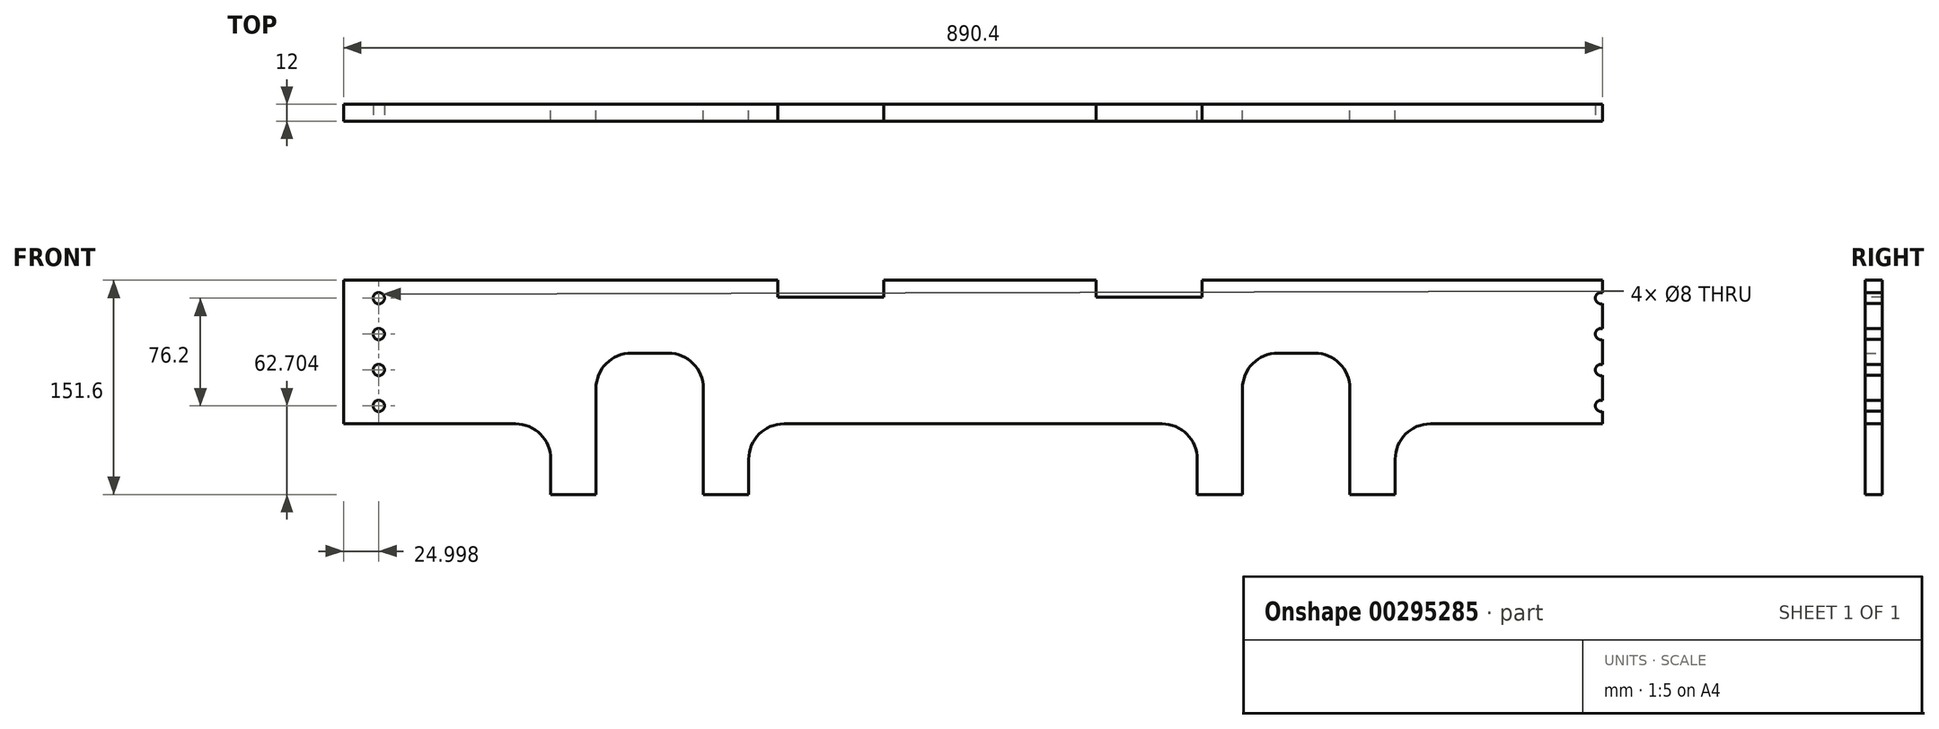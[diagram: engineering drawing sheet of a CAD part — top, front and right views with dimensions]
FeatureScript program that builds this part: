
annotation { "Feature Type Name" : "Feature", "Feature Type Description" : "" }
export const myFeature = defineFeature(function(context is Context, id is Id, definition is map)
    precondition{}
    {
        {
            var Q0;
            Q0=qCreatedBy(makeId("Front.planeOp"),FACE);
            var sketch = newSketch(context, id + "F0", { "sketchPlane" : qUnion([Q0])});
            skLineSegment(sketch, "E0", {"start": v(-558, 96.8) * mm, "end": v(332.4, 96.8) * mm});
            skLineSegment(sketch, "E1", {"start": v(332.4, 96.8) * mm, "end": v(332.4, -4.8) * mm});
            skLineSegment(sketch, "E2", {"start": v(332.4, -4.8) * mm, "end": v(210.8, -4.8) * mm});
            skLineSegment(sketch, "E3", {"start": v(185.8, -29.8) * mm, "end": v(185.8, -54.8) * mm});
            skLineSegment(sketch, "E4", {"start": v(185.8, -54.8) * mm, "end": v(153.8, -54.8) * mm});
            skLineSegment(sketch, "E5", {"start": v(153.8, -54.8) * mm, "end": v(153.8, 20.2) * mm});
            skLineSegment(sketch, "E6", {"start": v(128.8, 45.2) * mm, "end": v(102.8, 45.2) * mm});
            skLineSegment(sketch, "E7", {"start": v(77.8, 20.2) * mm, "end": v(77.8, -54.8) * mm});
            skLineSegment(sketch, "E8", {"start": v(77.8, -54.8) * mm, "end": v(45.8, -54.8) * mm});
            skLineSegment(sketch, "E9", {"start": v(-303.4, -54.8) * mm, "end": v(-303.4, 20.2) * mm});
            skLineSegment(sketch, "E10", {"start": v(-328.4, 45.2) * mm, "end": v(-354.4, 45.2) * mm});
            skLineSegment(sketch, "E11", {"start": v(-379.4, 20.2) * mm, "end": v(-379.4, -54.8) * mm});
            skLineSegment(sketch, "E12", {"start": v(-379.4, -54.8) * mm, "end": v(-411.4, -54.8) * mm});
            skLineSegment(sketch, "E13", {"start": v(-411.4, -54.8) * mm, "end": v(-411.4, -29.8) * mm});
            skLineSegment(sketch, "E14", {"start": v(-558, -4.8) * mm, "end": v(-558, 96.8) * mm});
            skPoint(sketch, "E15.visualSharp", {"position": v(-303.4, 45.2) * mm});
            skArc(sketch, "E15.filletArc", {"start": v(-303.4, 20.2) * mm, "mid": v(-310.72, 37.87) * mm, "end": v(-328.4, 45.2) * mm});
            skPoint(sketch, "E16.visualSharp", {"position": v(-379.4, 45.2) * mm});
            skArc(sketch, "E16.filletArc", {"start": v(-354.4, 45.2) * mm, "mid": v(-372.08, 37.87) * mm, "end": v(-379.4, 20.2) * mm});
            skPoint(sketch, "E17.visualSharp", {"position": v(185.8, -4.8) * mm});
            skArc(sketch, "E17.filletArc", {"start": v(210.8, -4.8) * mm, "mid": v(193.12, -12.13) * mm, "end": v(185.8, -29.8) * mm});
            skPoint(sketch, "E18.visualSharp", {"position": v(153.8, 45.2) * mm});
            skArc(sketch, "E18.filletArc", {"start": v(153.8, 20.2) * mm, "mid": v(146.48, 37.87) * mm, "end": v(128.8, 45.2) * mm});
            skPoint(sketch, "E19.visualSharp", {"position": v(77.8, 45.2) * mm});
            skArc(sketch, "E19.filletArc", {"start": v(102.8, 45.2) * mm, "mid": v(85.12, 37.87) * mm, "end": v(77.8, 20.2) * mm});
            skLineSegment(sketch, "E20", {"start": v(-558, -4.8) * mm, "end": v(-436.4, -4.8) * mm});
            skPoint(sketch, "E21.visualSharp", {"position": v(-411.4, -4.8) * mm});
            skArc(sketch, "E21.filletArc", {"start": v(-411.4, -29.8) * mm, "mid": v(-418.72, -12.13) * mm, "end": v(-436.4, -4.8) * mm});
            skLineSegment(sketch, "E22", {"start": v(-271.4, -54.8) * mm, "end": v(-271.4, -29.8) * mm});
            skLineSegment(sketch, "E23", {"start": v(-246.4, -4.8) * mm, "end": v(20.8, -4.8) * mm});
            skLineSegment(sketch, "E24", {"start": v(45.8, -29.8) * mm, "end": v(45.8, -54.8) * mm});
            skLineSegment(sketch, "E25.trimOffspring", {"start": v(-271.4, -54.8) * mm, "end": v(-303.4, -54.8) * mm});
            skPoint(sketch, "E26.visualSharp", {"position": v(-271.4, -4.8) * mm});
            skArc(sketch, "E26.filletArc", {"start": v(-246.4, -4.8) * mm, "mid": v(-264.08, -12.13) * mm, "end": v(-271.4, -29.8) * mm});
            skPoint(sketch, "E27.visualSharp", {"position": v(45.8, -4.8) * mm});
            skArc(sketch, "E27.filletArc", {"start": v(45.8, -29.8) * mm, "mid": v(38.48, -12.13) * mm, "end": v(20.8, -4.8) * mm});
            skSolve(sketch);
        }
        {
            var Q0;
            Q0=makeQuery(id+"F0.imprint","IMPRINT",FACE,{"disambiguationData":[TD([[makeQuery(id+"F0.imprint","IMPRINT",EDGE,{"derivedFrom":sQuery(id+"F0.wireOp",EDGE,"E0")}),-1.0]])]});
            extrude(context, id + "F1", {"entities" : qUnion([Q0]), "depth" : 12 * mm});
        }
        {
            var Q0;
            Q0=makeQuery(id+"F1.opExtrude","CAP_FACE",FACE,{"disambiguationData":[OSD([sQuery(id+"F0.wireOp",EDGE,"E0"),sQuery(id+"F0.wireOp",EDGE,"E1"),sQuery(id+"F0.wireOp",EDGE,"E2"),sQuery(id+"F0.wireOp",EDGE,"E3"),sQuery(id+"F0.wireOp",EDGE,"E4"),sQuery(id+"F0.wireOp",EDGE,"E5"),sQuery(id+"F0.wireOp",EDGE,"E6"),sQuery(id+"F0.wireOp",EDGE,"E7"),sQuery(id+"F0.wireOp",EDGE,"E8"),sQuery(id+"F0.wireOp",EDGE,"E9"),sQuery(id+"F0.wireOp",EDGE,"E10"),sQuery(id+"F0.wireOp",EDGE,"E11"),sQuery(id+"F0.wireOp",EDGE,"E12"),sQuery(id+"F0.wireOp",EDGE,"E13"),sQuery(id+"F0.wireOp",EDGE,"E14"),sQuery(id+"F0.wireOp",EDGE,"E15.filletArc"),sQuery(id+"F0.wireOp",EDGE,"E16.filletArc"),sQuery(id+"F0.wireOp",EDGE,"E17.filletArc"),sQuery(id+"F0.wireOp",EDGE,"E18.filletArc"),sQuery(id+"F0.wireOp",EDGE,"E19.filletArc"),sQuery(id+"F0.wireOp",EDGE,"E20"),sQuery(id+"F0.wireOp",EDGE,"E21.filletArc"),sQuery(id+"F0.wireOp",EDGE,"E22"),sQuery(id+"F0.wireOp",EDGE,"E23"),sQuery(id+"F0.wireOp",EDGE,"E24"),sQuery(id+"F0.wireOp",EDGE,"E25.trimOffspring"),sQuery(id+"F0.wireOp",EDGE,"E26.filletArc"),sQuery(id+"F0.wireOp",EDGE,"E27.filletArc")])],"isStart":false});
            var sketch = newSketch(context, id + "F2", { "sketchPlane" : qUnion([Q0])});
            skPoint(sketch, "E28", {"position": v(-533, 84.1) * mm});
            skPoint(sketch, "E29", {"position": v(-533, 58.7) * mm});
            skPoint(sketch, "E30", {"position": v(-533, 33.3) * mm});
            skPoint(sketch, "E31", {"position": v(-533, 7.9) * mm});
            skPoint(sketch, "E32", {"position": v(-395.4, -48.8) * mm});
            skPoint(sketch, "E33", {"position": v(-287.4, -48.8) * mm});
            skLineSegment(sketch, "E34", {"start": v(-100.8, -4.8) * mm, "end": v(-100.8, 96.8) * mm});
            skPoint(sketch, "E35.MirrorP", {"position": v(85.8, -48.8) * mm});
            skPoint(sketch, "E36.MirrorP", {"position": v(331.4, 58.7) * mm});
            skPoint(sketch, "E37.MirrorP", {"position": v(193.8, -48.8) * mm});
            skPoint(sketch, "E38.MirrorP", {"position": v(331.4, 84.1) * mm});
            skPoint(sketch, "E39.MirrorP", {"position": v(331.4, 7.9) * mm});
            skPoint(sketch, "E40.MirrorP", {"position": v(331.4, 33.3) * mm});
            skSolve(sketch);
        }
        {
            var Q0;
            Q0=sQuery(id+"F2.wireOp",VERTEX,"E28");
            var Q1;
            Q1=sQuery(id+"F2.wireOp",VERTEX,"E29");
            var Q2;
            Q2=sQuery(id+"F2.wireOp",VERTEX,"E30");
            var Q3;
            Q3=sQuery(id+"F2.wireOp",VERTEX,"E31");
            var Q4;
            Q4=sQuery(id+"F2.wireOp",VERTEX,"E38.MirrorP");
            var Q5;
            Q5=sQuery(id+"F2.wireOp",VERTEX,"E36.MirrorP");
            var Q6;
            Q6=sQuery(id+"F2.wireOp",VERTEX,"E40.MirrorP");
            var Q7;
            Q7=sQuery(id+"F2.wireOp",VERTEX,"E39.MirrorP");
            var Q8;
            Q8=makeQuery(id+"F1.opExtrude","SWEPT_BODY",BODY,{"disambiguationData":[OSD([sQuery(id+"F0.wireOp",EDGE,"E0"),sQuery(id+"F0.wireOp",EDGE,"E1"),sQuery(id+"F0.wireOp",EDGE,"E2"),sQuery(id+"F0.wireOp",EDGE,"E3"),sQuery(id+"F0.wireOp",EDGE,"E4"),sQuery(id+"F0.wireOp",EDGE,"E5"),sQuery(id+"F0.wireOp",EDGE,"E6"),sQuery(id+"F0.wireOp",EDGE,"E7"),sQuery(id+"F0.wireOp",EDGE,"E8"),sQuery(id+"F0.wireOp",EDGE,"E9"),sQuery(id+"F0.wireOp",EDGE,"E10"),sQuery(id+"F0.wireOp",EDGE,"E11"),sQuery(id+"F0.wireOp",EDGE,"E12"),sQuery(id+"F0.wireOp",EDGE,"E13"),sQuery(id+"F0.wireOp",EDGE,"E14"),sQuery(id+"F0.wireOp",EDGE,"E15.filletArc"),sQuery(id+"F0.wireOp",EDGE,"E16.filletArc"),sQuery(id+"F0.wireOp",EDGE,"E17.filletArc"),sQuery(id+"F0.wireOp",EDGE,"E18.filletArc"),sQuery(id+"F0.wireOp",EDGE,"E19.filletArc"),sQuery(id+"F0.wireOp",EDGE,"E20"),sQuery(id+"F0.wireOp",EDGE,"E21.filletArc"),sQuery(id+"F0.wireOp",EDGE,"E22"),sQuery(id+"F0.wireOp",EDGE,"E23"),sQuery(id+"F0.wireOp",EDGE,"E24"),sQuery(id+"F0.wireOp",EDGE,"E25.trimOffspring"),sQuery(id+"F0.wireOp",EDGE,"E26.filletArc"),sQuery(id+"F0.wireOp",EDGE,"E27.filletArc")])]});
            hole(context, id + "F3", {"style" : HoleStyle.SIMPLE, "endStyle" : HoleEndStyle.THROUGH, "standardTappedOrClearance" : lookupTablePath({ "standard" : "ISO", "size" : "8", "type" : "Drilled" }), "standardBlindInLast" : lookupTablePath({ "standard" : "ISO", "size" : "8", "type" : "Drilled" }), "holeDiameter" : 8 * mm, "tappedDepth" : 12 * mm, "tapClearance" : 3, "locations" : qUnion([Q0, Q1, Q2, Q3, Q4, Q5, Q6, Q7]), "scope" : qUnion([Q8])});
        }
        {
            var Q0;
            Q0=makeQuery(id+"F1.opExtrude","CAP_FACE",FACE,{"disambiguationData":[OSD([sQuery(id+"F0.wireOp",EDGE,"E0"),sQuery(id+"F0.wireOp",EDGE,"E1"),sQuery(id+"F0.wireOp",EDGE,"E2"),sQuery(id+"F0.wireOp",EDGE,"E3"),sQuery(id+"F0.wireOp",EDGE,"E4"),sQuery(id+"F0.wireOp",EDGE,"E5"),sQuery(id+"F0.wireOp",EDGE,"E6"),sQuery(id+"F0.wireOp",EDGE,"E7"),sQuery(id+"F0.wireOp",EDGE,"E8"),sQuery(id+"F0.wireOp",EDGE,"E9"),sQuery(id+"F0.wireOp",EDGE,"E10"),sQuery(id+"F0.wireOp",EDGE,"E11"),sQuery(id+"F0.wireOp",EDGE,"E12"),sQuery(id+"F0.wireOp",EDGE,"E13"),sQuery(id+"F0.wireOp",EDGE,"E14"),sQuery(id+"F0.wireOp",EDGE,"E15.filletArc"),sQuery(id+"F0.wireOp",EDGE,"E16.filletArc"),sQuery(id+"F0.wireOp",EDGE,"E17.filletArc"),sQuery(id+"F0.wireOp",EDGE,"E18.filletArc"),sQuery(id+"F0.wireOp",EDGE,"E19.filletArc"),sQuery(id+"F0.wireOp",EDGE,"E20"),sQuery(id+"F0.wireOp",EDGE,"E21.filletArc"),sQuery(id+"F0.wireOp",EDGE,"E22"),sQuery(id+"F0.wireOp",EDGE,"E23"),sQuery(id+"F0.wireOp",EDGE,"E24"),sQuery(id+"F0.wireOp",EDGE,"E25.trimOffspring"),sQuery(id+"F0.wireOp",EDGE,"E26.filletArc"),sQuery(id+"F0.wireOp",EDGE,"E27.filletArc")])],"isStart":false});
            var sketch = newSketch(context, id + "F4", { "sketchPlane" : qUnion([Q0])});
            skLineSegment(sketch, "E41.bottom", {"start": v(-250.8, 96.8) * mm, "end": v(-175.8, 96.8) * mm});
            skLineSegment(sketch, "E41.top", {"start": v(-250.8, 84.8) * mm, "end": v(-175.8, 84.8) * mm});
            skLineSegment(sketch, "E41.left", {"start": v(-250.8, 96.8) * mm, "end": v(-250.8, 84.8) * mm});
            skLineSegment(sketch, "E41.right", {"start": v(-175.8, 96.8) * mm, "end": v(-175.8, 84.8) * mm});
            skLineSegment(sketch, "E42.bottom", {"start": v(-25.8, 96.8) * mm, "end": v(49.2, 96.8) * mm});
            skLineSegment(sketch, "E42.top", {"start": v(-25.8, 84.8) * mm, "end": v(49.2, 84.8) * mm});
            skLineSegment(sketch, "E42.left", {"start": v(-25.8, 96.8) * mm, "end": v(-25.8, 84.8) * mm});
            skLineSegment(sketch, "E42.right", {"start": v(49.2, 96.8) * mm, "end": v(49.2, 84.8) * mm});
            skSolve(sketch);
        }
        {
            var Q0;
            Q0 = qSketchRegion(id + "F4", true);
            extrude(context, id + "F5", {"entities" : qUnion([Q0]), "operationType" : NewBodyOperationType.REMOVE, "oppositeDirection" : true, "depth" : 25 * mm});
        }
    });
